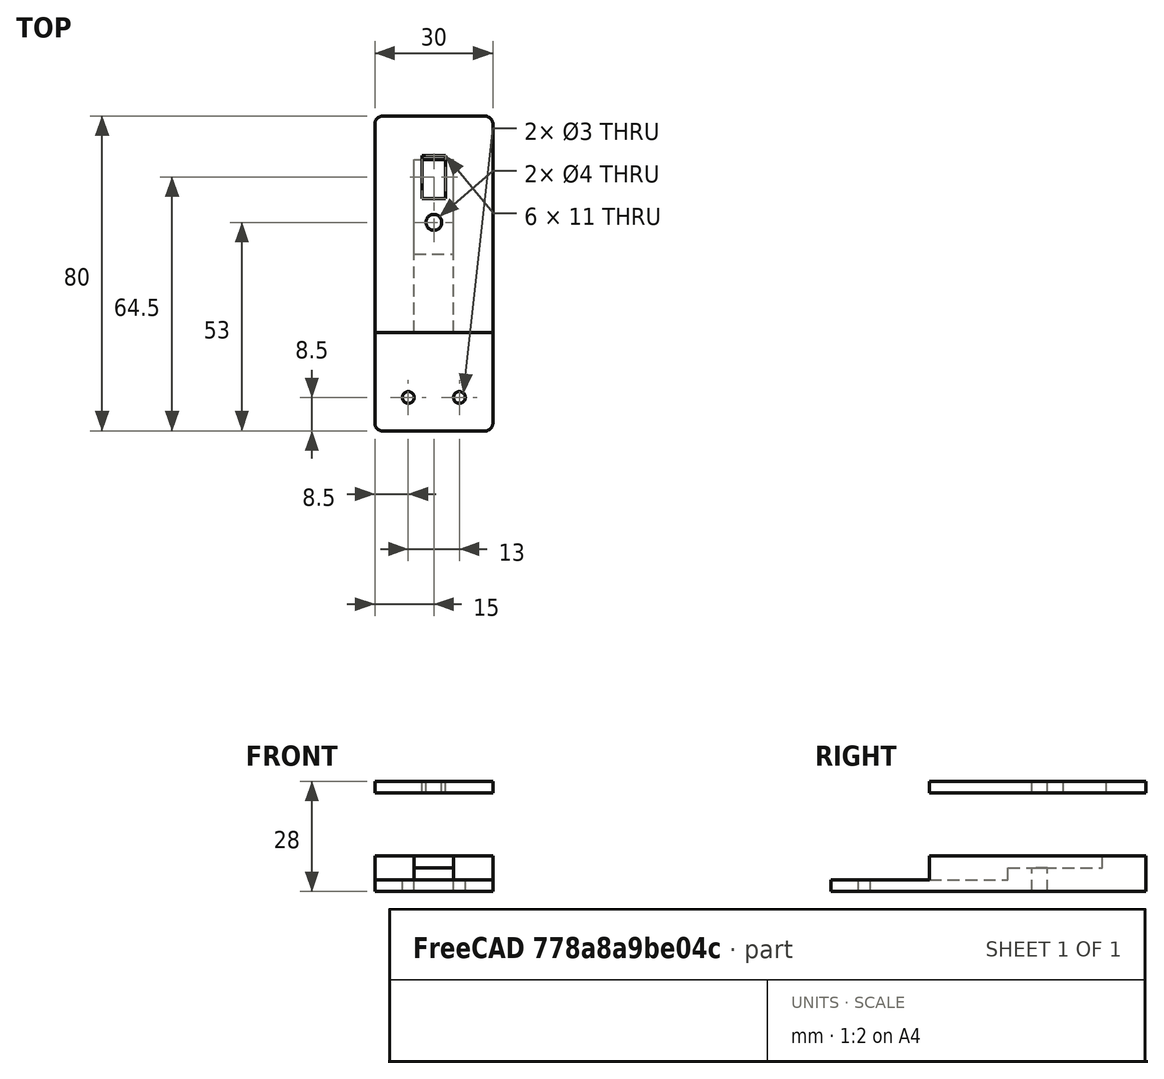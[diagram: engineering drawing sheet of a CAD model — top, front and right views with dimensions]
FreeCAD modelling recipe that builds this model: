
FCSTD DOCUMENT  (FreeCAD 0.15R4671 (Git))
Label: SensorTracker
License: All rights reserved
LicenseURL: http://en.wikipedia.org/wiki/All_rights_reserved
objects: Part::Cut×7, Part::Box×6, Part::Fillet×6, Part::Cylinder×4, Part::MultiFuse×1
note: 24 computed .brp shape members not serialized (recipe doc carries the construction recipe); baked Part::Feature solids carry a one-line shape summary decoded from their .brp

FEATURE [Part::Box] Box  label="Cubo"
  Height = 9
  Length = 30
  Width = 80
FEATURE [Part::Box] Box001  label="Cubo001"
  Height = 3
  Length = 10
  Placement = pos=(10,25,6) rot=(0,0,1;0rad)
  Width = 44
FEATURE [Part::Cut] Cut
  Base = -> Box
  Tool = -> Box001
FEATURE [Part::Box] Box002  label="Cubo002"
  Height = 3
  Length = 10
  Placement = pos=(10,25,3) rot=(0,0,1;0rad)
  Width = 20
FEATURE [Part::Cut] Cut001
  Base = -> Cut
  Tool = -> Box002
FEATURE [Part::Box] Box003  label="Cubo003"
  Height = 6
  Length = 30
  Placement = pos=(0,0,3) rot=(0,0,1;0rad)
  Width = 25
FEATURE [Part::Cut] Cut002
  Base = -> Cut001
  Tool = -> Box003
FEATURE [Part::Cylinder] Cylinder  label="Cilindro"
  Angle = 360
  Height = 6
  Placement = pos=(15,53,0) rot=(0,0,1;0rad)
  Radius = 2
FEATURE [Part::Cut] Cut003
  Base = -> Cut002
  Tool = -> Cylinder
FEATURE [Part::Cylinder] Cylinder001  label="Cilindro001"
  Angle = 360
  Height = 3
  Placement = pos=(8.5,8.5,0) rot=(0,0,1;0rad)
  Radius = 1.5
FEATURE [Part::Cylinder] Cylinder002  label="Cilindro002"
  Angle = 360
  Height = 3
  Placement = pos=(21.5,8.5,0) rot=(0,0,1;0rad)
  Radius = 1.5
FEATURE [Part::MultiFuse] Fusion
  Shapes = -> [Cylinder002,Cylinder001]
FEATURE [Part::Cut] Cut004
  Base = -> Cut003
  Tool = -> Fusion
FEATURE [Part::Fillet] Fillet
  Base = -> Cut004
  Edges = 1 edges r=2: [Edge7]
FEATURE [Part::Fillet] Fillet001
  Base = -> Fillet
  Edges = 1 edges r=2: [Edge3]
FEATURE [Part::Fillet] Fillet002
  Base = -> Fillet001
  Edges = 1 edges r=2: [Edge29]
FEATURE [Part::Fillet] Fillet003
  Base = -> Fillet002
  Edges = 1 edges r=2: [Edge20]
FEATURE [Part::Box] Box004  label="Cubo004"
  Height = 3
  Length = 6
  Placement = pos=(12,59,25) rot=(0,0,1;0rad)
  Width = 11
FEATURE [Part::Box] Box005  label="Cubo005"
  Height = 3
  Length = 30
  Placement = pos=(0,25,25) rot=(0,0,1;0rad)
  Width = 55
FEATURE [Part::Cut] Cut005
  Base = -> Box005
  Tool = -> Box004
FEATURE [Part::Cylinder] Cylinder003  label="Cilindro003"
  Angle = 360
  Height = 3
  Placement = pos=(15,53,25) rot=(0,0,1;0rad)
  Radius = 2
FEATURE [Part::Cut] Cut006
  Base = -> Cut005
  Tool = -> Cylinder003
FEATURE [Part::Fillet] Fillet004
  Base = -> Cut006
  Edges = 1 edges r=2: [Edge16]
FEATURE [Part::Fillet] Fillet005
  Base = -> Fillet004
  Edges = 1 edges r=2: [Edge13]
